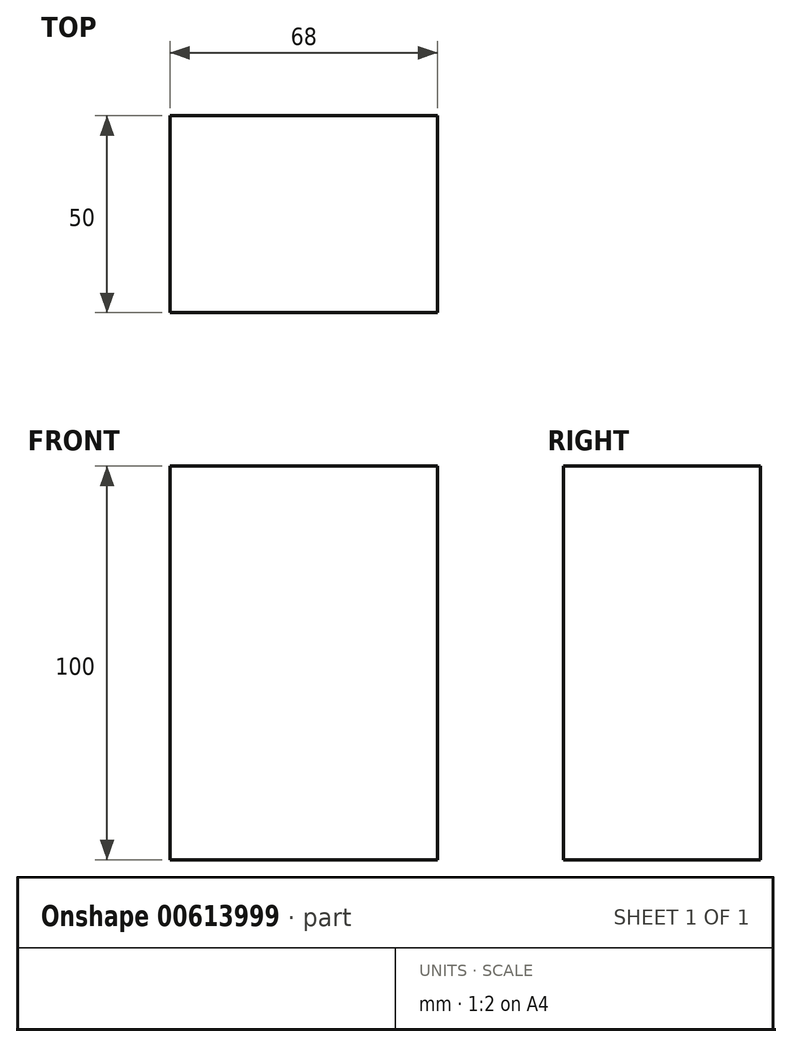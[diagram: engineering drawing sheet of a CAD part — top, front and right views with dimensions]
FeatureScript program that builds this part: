
annotation { "Feature Type Name" : "Feature", "Feature Type Description" : "" }
export const myFeature = defineFeature(function(context is Context, id is Id, definition is map)
    precondition{}
    {
        {
            var Q0;
            Q0=qCreatedBy(makeId("Front.planeOp"),FACE);
            var sketch = newSketch(context, id + "F0", { "sketchPlane" : qUnion([Q0])});
            skLineSegment(sketch, "E0.bottom", {"start": v(-34, 50) * mm, "end": v(34, 50) * mm});
            skLineSegment(sketch, "E0.top", {"start": v(-34, -50) * mm, "end": v(34, -50) * mm});
            skLineSegment(sketch, "E0.left", {"start": v(-34, 50) * mm, "end": v(-34, -50) * mm});
            skLineSegment(sketch, "E0.right", {"start": v(34, 50) * mm, "end": v(34, -50) * mm});
            skPoint(sketch, "E0.middle", {"position": v(0, 0) * mm});
            skSolve(sketch);
        }
        {
            var Q0;
            Q0=makeQuery(id+"F0.imprint","IMPRINT",FACE,{"disambiguationData":[TD([[makeQuery(id+"F0.imprint","IMPRINT",EDGE,{"derivedFrom":sQuery(id+"F0.wireOp",EDGE,"E0.bottom")}),-1.0]])]});
            extrude(context, id + "F1", {"entities" : qUnion([Q0]), "depth" : 50 * mm, "offsetDistance" : 25 * mm});
        }
    });
